# Revit family: Support Beam
name_source: partatom
category: Generic Models
revit_build: Autodesk Revit 2016 (Build: 20150220_1215(x64)
units: mm (PartAtom-declared; Revit-internal decimal feet)

## family parameters
Always vertical = Yes
Can host rebar = No
Cut with Voids When Loaded = No
Part Type = Normal
Room Calculation Point = No
Round Connector Dimension = Use Diameter
Shared = No
Work Plane-Based = No

## types (3) — shared parameters

## per-type parameters (varying)
| type | Braced | Cantilever | Hung | Mounting Height | Support Length |
| Hung Support | No | No | Yes | 1060 mm | 450 mm  [stored 1.47638 ft] |
| Braced Support | Yes | No | No | 1500 mm  [stored 4.92126 ft] | 450 mm  [stored 1.47638 ft] |
| Cantilever Support | No | Yes | No | 1060 mm | 750 mm |

note: [stored X ft] marks values corroborated as IEEE doubles in the binary element streams (Revit-internal decimal feet)

## geometry (parser evidence)
native form markers: Sweep x3
no freeform markers — native parametric forms only
